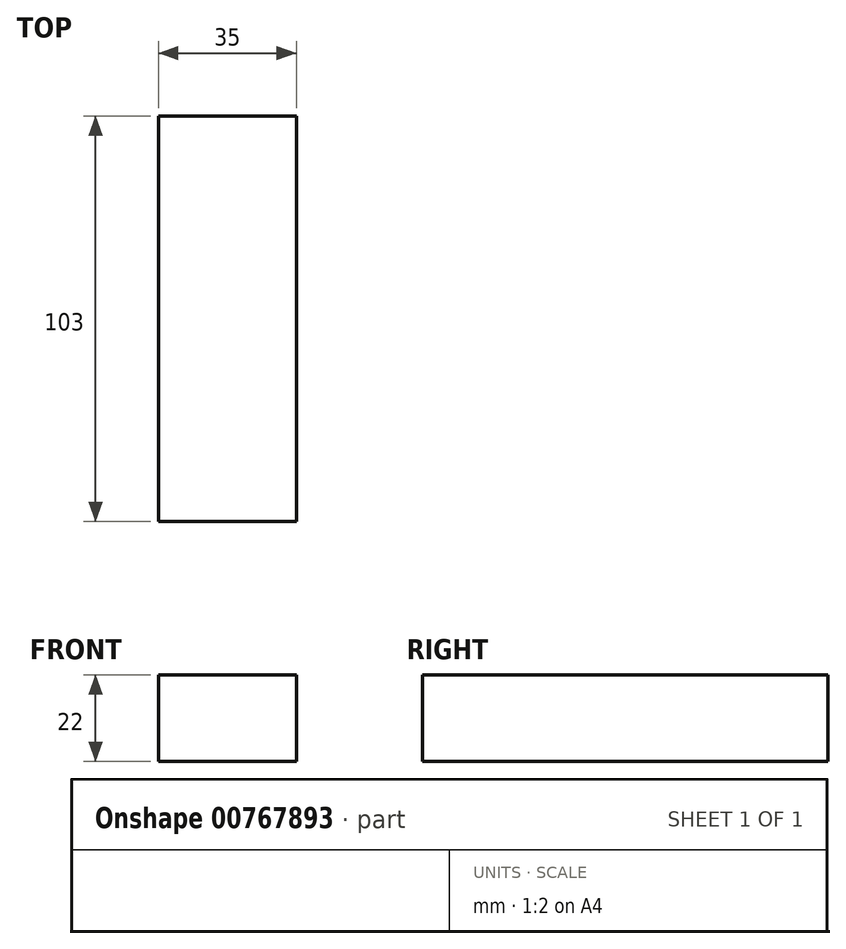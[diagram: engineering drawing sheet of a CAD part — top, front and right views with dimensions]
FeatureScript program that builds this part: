
annotation { "Feature Type Name" : "Feature", "Feature Type Description" : "" }
export const myFeature = defineFeature(function(context is Context, id is Id, definition is map)
    precondition{}
    {
        {
            var Q0;
            Q0=qCreatedBy(makeId("Top.planeOp"),FACE);
            var sketch = newSketch(context, id + "F0", { "sketchPlane" : qUnion([Q0])});
            skLineSegment(sketch, "E0.bottom", {"start": v(17.5, -51.5) * mm, "end": v(-17.5, -51.5) * mm});
            skLineSegment(sketch, "E0.top", {"start": v(17.5, 51.5) * mm, "end": v(-17.5, 51.5) * mm});
            skLineSegment(sketch, "E0.left", {"start": v(17.5, -51.5) * mm, "end": v(17.5, 51.5) * mm});
            skLineSegment(sketch, "E0.right", {"start": v(-17.5, -51.5) * mm, "end": v(-17.5, 51.5) * mm});
            skPoint(sketch, "E0.middle", {"position": v(0, 0) * mm});
            skSolve(sketch);
        }
        {
            var Q0;
            Q0=makeQuery(id+"F0.imprint","IMPRINT",FACE,{"disambiguationData":[TD([[makeQuery(id+"F0.imprint","IMPRINT",EDGE,{"derivedFrom":sQuery(id+"F0.wireOp",EDGE,"E0.bottom")}),-1.0]])]});
            extrude(context, id + "F1", {"entities" : qUnion([Q0]), "depth" : 22 * mm, "offsetDistance" : 25 * mm});
        }
    });
